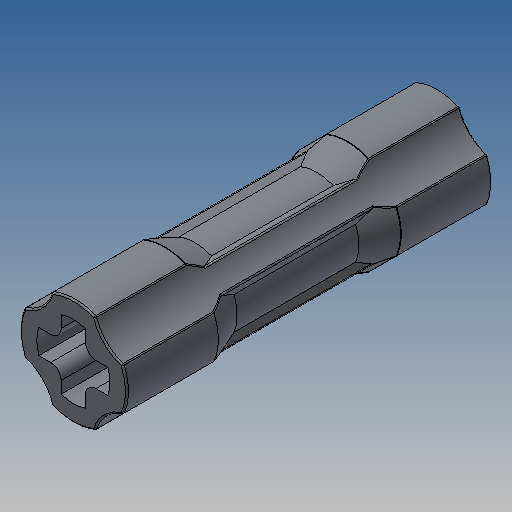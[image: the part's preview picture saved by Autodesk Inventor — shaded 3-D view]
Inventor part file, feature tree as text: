
AUTODESK INVENTOR PART (.ipt)
format: ipt  version: 2025 (Build 290162010, 162A)  size: 545,792 bytes
history: native  units: in
note: dims shown in document units (in); Inventor stores cm internally (conversion verified against a paired STEP export)
features: extrude x4, sketch x3, revolve x1, pattern_circular x1, fillet x1
ambient origin geometry x8: Origin, YZ Plane, XZ Plane, XY Plane, X Axis, Y Axis, Z Axis, Center Point
bodies: Solid1 (feature_tree)
feature tree (10):
  revolve  "Revolution1"  [1 undecoded]
  sketch  "Sketch3"  dims[d2=0.9449in d3=0.315in]
  extrude  "Extrusion1"  Depth=0.315in
  extrude  "Extrusion2"  TaperAngle=90.0deg  [1 undecoded]
  sketch  "Sketch4"  dims[d4=0.2772in d5=90.0deg d6=0.2126in d7=0.315in d9=0.0609in d10=0.0831in d11=0.3937in d12=0.0in d13=0.3937in d14=0.0in d15=0.189in d16=0.0315in d17=0.063in d18=0.063in d19=0.0315in d23=0.0945in d26=0.1113in d27=0.0315in d29=0.315in d30=0.0in d31=0.7874in d32=360.0deg d34=0.315in d35=0.0in d36=0.0039in d37=0.0in d38=0.0in d39=0.0in d40=0.0315in]
  extrude  "Extrusion3"  Depth=0.0039in
  pattern_circular  "Circular Pattern1"  [2 undecoded]
  extrude  "Extrusion4"  Depth=0.0039in
  fillet  "Fillet1"  Radius=0.0831in
  sketch  "Sketch2"  dims[d0=0.2173in d1=0.2362in]
note: 4 required parameter values undecoded (feature->parameter linkage not recoverable at this tier; creation-order binding heuristic only, values carry confidence <= 0.55)